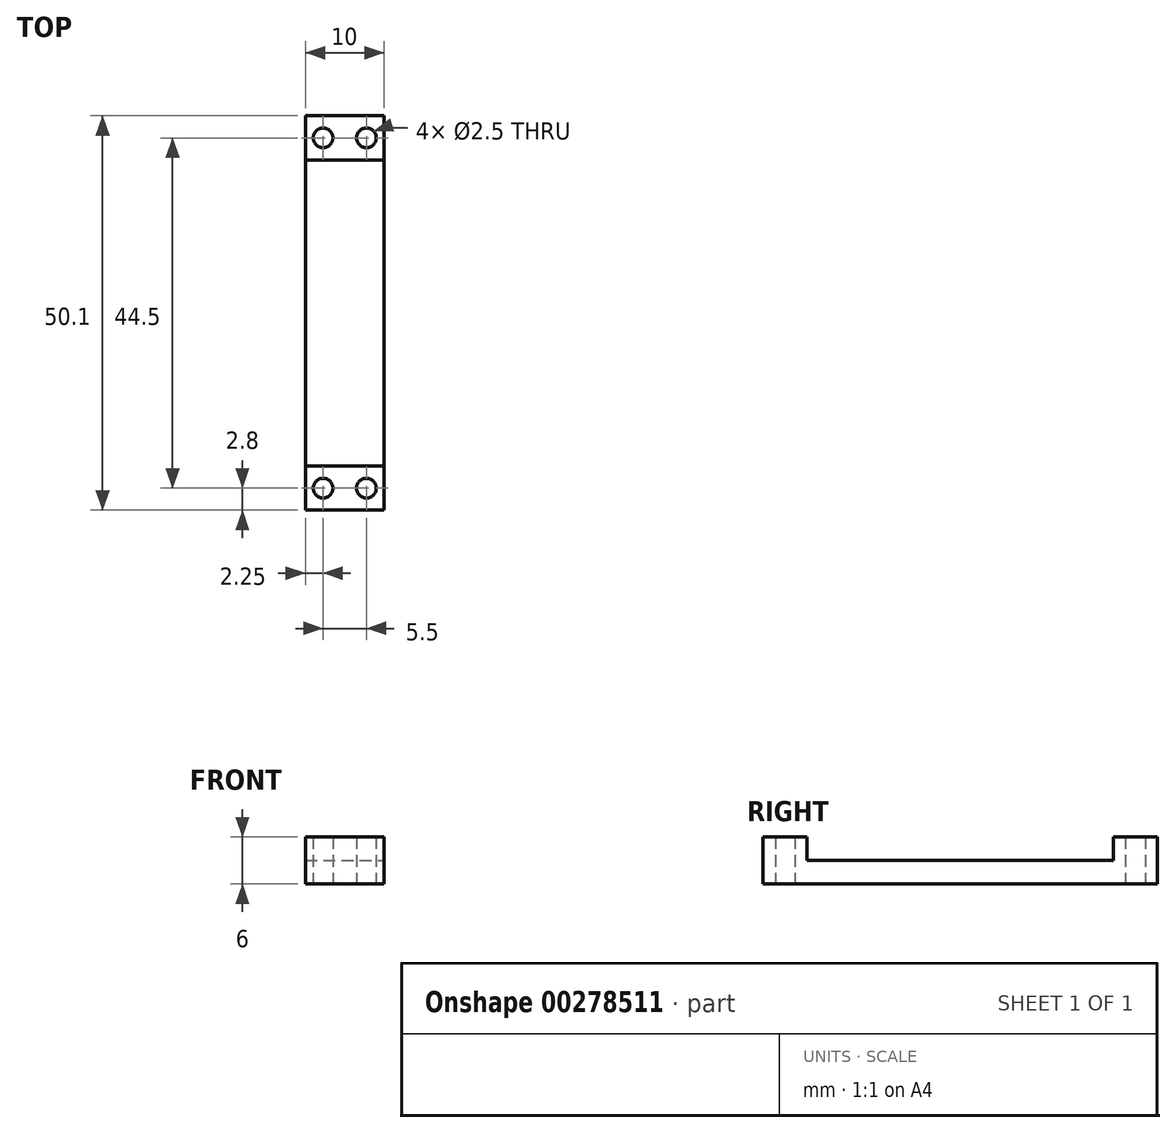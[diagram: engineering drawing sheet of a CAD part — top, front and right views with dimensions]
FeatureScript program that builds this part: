
annotation { "Feature Type Name" : "Feature", "Feature Type Description" : "" }
export const myFeature = defineFeature(function(context is Context, id is Id, definition is map)
    precondition{}
    {
        {
            var Q0;
            Q0=qCreatedBy(makeId("Top.planeOp"),FACE);
            var sketch = newSketch(context, id + "F0", { "sketchPlane" : qUnion([Q0])});
            skLineSegment(sketch, "E0.bottom", {"start": v(-5, 25.05) * mm, "end": v(5, 25.05) * mm});
            skLineSegment(sketch, "E0.top", {"start": v(-5, -25.05) * mm, "end": v(5, -25.05) * mm});
            skLineSegment(sketch, "E0.left", {"start": v(-5, 25.05) * mm, "end": v(-5, -25.05) * mm});
            skLineSegment(sketch, "E0.right", {"start": v(5, 25.05) * mm, "end": v(5, -25.05) * mm});
            skPoint(sketch, "E0.middle", {"position": v(0, 0) * mm});
            skCircle(sketch, "E1", {"center": v(-2.75, 22.25) * mm, "radius": 1.25 * mm});
            skCircle(sketch, "E2.MirrorC", {"center": v(-2.75, -22.25) * mm, "radius": 1.25 * mm});
            skCircle(sketch, "E3.MirrorC", {"center": v(2.75, 22.25) * mm, "radius": 1.25 * mm});
            skCircle(sketch, "E4.MirrorC", {"center": v(2.75, -22.25) * mm, "radius": 1.25 * mm});
            skLineSegment(sketch, "E5", {"start": v(2.75, 22.25) * mm, "end": v(-2.75, 22.25) * mm, "construction": true});
            skLineSegment(sketch, "E6.MirrorCS", {"start": v(-5, 19.45) * mm, "end": v(5, 19.45) * mm});
            skLineSegment(sketch, "E7.MirrorCS", {"start": v(-5, -19.45) * mm, "end": v(5, -19.45) * mm});
            skSolve(sketch);
        }
        {
            var Q0;
            {var subQ0=sQuery(id+"F0.wireOp",EDGE,"E6.MirrorCS");Q0=makeQuery(id+"F0.imprint","IMPRINT",FACE,{"disambiguationData":[TD([[makeQuery(id+"F0.imprint","IMPRINT",EDGE,{"derivedFrom":subQ0}),-1.0]])]});}
            extrude(context, id + "F1", {"entities" : qUnion([Q0]), "depth" : 3 * mm});
        }
        {
            var Q0;
            {var subQ1=sQuery(id+"F0.wireOp",EDGE,"E0.bottom");Q0=makeQuery(id+"F0.imprint","IMPRINT",FACE,{"disambiguationData":[TD([[makeQuery(id+"F0.imprint","IMPRINT",EDGE,{"derivedFrom":subQ1}),-1.0]])]});}
            var Q1;
            {var subQ1=sQuery(id+"F0.wireOp",EDGE,"E0.top");Q1=makeQuery(id+"F0.imprint","IMPRINT",FACE,{"disambiguationData":[TD([[makeQuery(id+"F0.imprint","IMPRINT",EDGE,{"derivedFrom":subQ1}),1.0]])]});}
            extrude(context, id + "F2", {"entities" : qUnion([Q0, Q1]), "operationType" : NewBodyOperationType.ADD, "depth" : 6 * mm});
        }
    });
